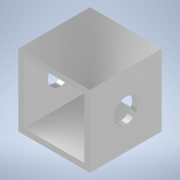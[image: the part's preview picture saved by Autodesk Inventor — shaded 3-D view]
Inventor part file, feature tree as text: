
AUTODESK INVENTOR PART (.ipt)
format: ipt  version: 2020.3 (Build 243373000, 373)  size: 111,104 bytes
history: native  units: mm
features: sketch x2, other x1, extrude x1, hole x1
ambient origin geometry x8: Origin, YZ Plane, XZ Plane, XY Plane, X Axis, Y Axis, Z Axis, Center Point
bodies: Body1 (feature_tree)
feature tree (5):
  other  "ソリッド1"
  extrude  "押し出し1"  Depth=15.0mm
  hole  "穴1"  [1 undecoded]
  sketch  "スケッチ1"
  sketch  "スケッチ2"
note: 1 required parameter value undecoded (feature->parameter linkage not recoverable at this tier; creation-order binding heuristic only, values carry confidence <= 0.55)
